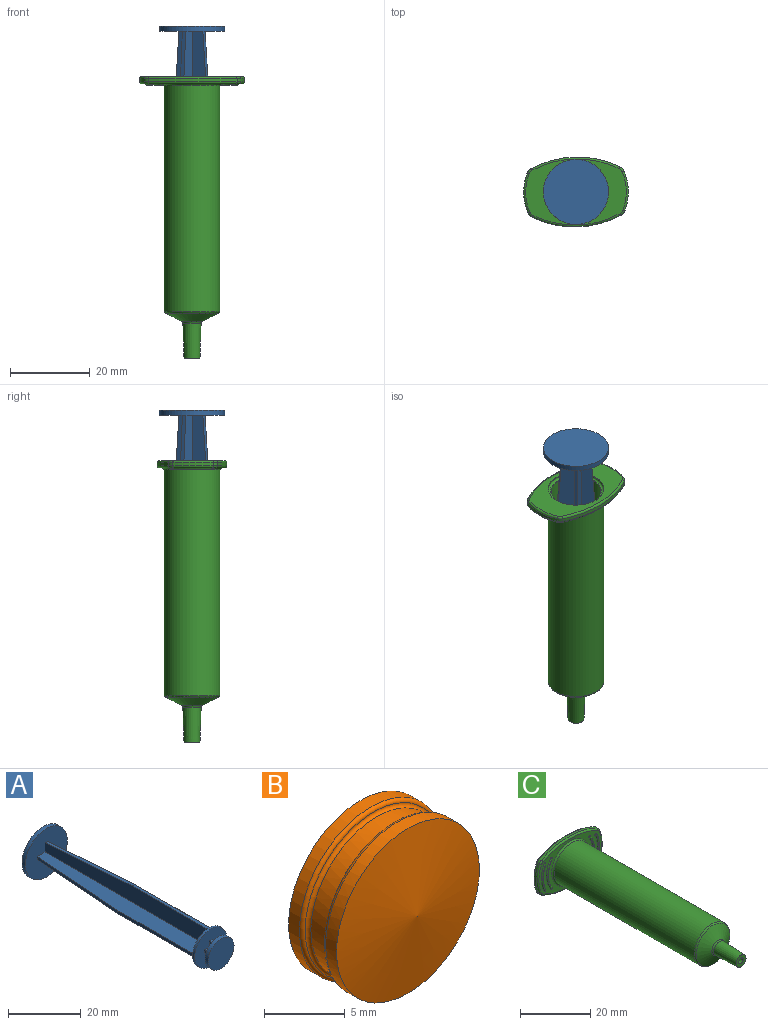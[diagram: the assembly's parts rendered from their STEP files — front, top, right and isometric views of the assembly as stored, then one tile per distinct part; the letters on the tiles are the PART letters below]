
ASSEMBLY  parts=3 mates=2
PART A: 37 faces, bbox 16.3x69x16.3 mm
  f0: plane 2.8x2mm, normal (-1,0,0), area 5.6mm2, adj f1,f10,f33,f34
  f1: plane 2.8x2mm, normal (0,0,-1), area 5.6mm2, adj f0,f11,f33,f34
  f2: plane 2.8x2mm, normal (0,0,-1), area 5.6mm2, adj f3,f9,f33,f34
  f3: plane 2.8x2mm, normal (1,0,0), area 5.6mm2, adj f2,f10,f33,f34
  f4: plane 2.8x2mm, normal (1,0,0), area 5.6mm2, adj f5,f8,f33,f34
  f5: plane 2.8x2mm, normal (0,0,1), area 5.6mm2, adj f4,f9,f33,f34
  f6: plane 2.8x2mm, normal (-1,0,0), area 5.6mm2, adj f7,f8,f33,f34
  f7: plane 2.8x2mm, normal (0,0,1), area 5.6mm2, adj f6,f11,f33,f34
  f8: plane 2.8x1mm, normal (0,0,1), area 2.8mm2, adj f4,f6,f33,f34
  f9: plane 2.8x1mm, normal (1,0,0), area 2.8mm2, adj f2,f5,f33,f34
  f10: plane 2.8x1mm, normal (0,0,-1), area 2.8mm2, adj f0,f3,f33,f34
  f11: plane 2.8x1mm, normal (-1,0,0), area 2.8mm2, adj f1,f7,f33,f34
  f12: plane 62.95x5.5mm, normal (0,0,1), area 305.7mm2, adj f15,f20,f24,f28,f32
  f13: plane 62.95x5.5mm, normal (0,0,-1), area 305.7mm2, adj f14,f20,f24,f28,f32
  f14: plane 62.95x5.5mm, normal (-1,0,0), area 305.7mm2, adj f13,f21,f25,f28,f32
  f15: plane 62.95x5.5mm, normal (-1,0,0), area 305.7mm2, adj f12,f23,f27,f28,f32
  f16: plane 62.95x5.5mm, normal (1,0,0), area 305.7mm2, adj f17,f21,f25,f28,f32
  f17: plane 62.95x5.5mm, normal (0,0,-1), area 305.7mm2, adj f16,f22,f26,f28,f32
  f18: plane 62.95x5.5mm, normal (0,0,1), area 305.7mm2, adj f19,f22,f26,f28,f32
  f19: plane 62.95x5.5mm, normal (1,0,0), area 305.7mm2, adj f18,f23,f27,f28,f32
  f20: plane 29.25x1mm, normal (-1,0,0), area 29.2mm2, adj f12,f13,f24,f32
  f21: plane 29.25x1mm, normal (0,0,-1), area 29.2mm2, adj f14,f16,f25,f32
  f22: plane 29.25x1mm, normal (1,0,0), area 29.2mm2, adj f17,f18,f26,f32
  f23: plane 29.25x1mm, normal (0,0,1), area 29.2mm2, adj f15,f19,f27,f32
  f24: plane 33.7x2.41mm, normal (-1,0.07,0), area 33.8mm2, adj f12,f13,f20,f28
  f25: plane 33.7x2.41mm, normal (0,0.07,-1), area 33.8mm2, adj f14,f16,f21,f28
  f26: plane 33.7x2.41mm, normal (1,0.07,0), area 33.8mm2, adj f17,f18,f22,f28
  f27: plane 33.7x2.41mm, normal (0,0.07,1), area 33.8mm2, adj f15,f19,f23,f28
  f28: plane 16.3x16.3mm, normal (0,-1,0), area 195.3mm2, adj f12,f13,f14,f15,f16,f17,f18,f19
  f29: cylinder r=8.15mm len=16.3mm, axis (0,1,0), area 66.6mm2, adj f28,f30
  f30: plane 16.3x16.3mm, normal (0,1,0), area 208.7mm2, adj f29
  f31: cylinder r=6.25mm len=12.5mm, axis (0,-1,0), area 29.5mm2, adj f32,f33
  f32: plane 12.5x12.5mm, normal (0,1,0), area 99.7mm2, adj f12,f13,f14,f15,f16,f17,f18,f19
  f33: plane 12.5x12.5mm, normal (0,-1,0), area 113.7mm2, adj f0,f1,f2,f3,f4,f5,f6,f7
  f34: plane 10x10mm, normal (0,1,0), area 69.5mm2, adj f0,f1,f2,f3,f4,f5,f6,f7
  f35: cylinder r=5mm len=10mm, axis (0,-1,0), area 37.7mm2, adj f34,f36
  f36: plane 10x10mm, normal (0,-1,0), area 78.5mm2, adj f35
PART B: 13 faces, bbox 13.5x5x13.5 mm
  f0: cone r=0mm half-angle=82.7deg, axis (0,1,0), area 123.7mm2, adj f1
  f1: cylinder r=6.25mm len=12.5mm, axis (0,-1,0), area 37.3mm2, adj f0,f10
  f2: cylinder r=5.75mm len=11.5mm, axis (0,-1,0), area 47mm2, adj f9,f12
  f3: cylinder r=6.25mm len=12.5mm, axis (0,-1,0), area 37.3mm2, adj f4,f11
  f4: plane 12.5x12.5mm, normal (0,1,0), area 103.1mm2, adj f3,f5
  f5: cylinder r=2.5mm len=5mm, axis (0,-1,0), area 44mm2, adj f4,f6
  f6: plane 10x10mm, normal (0,-1,0), area 58.9mm2, adj f5,f7
  f7: cylinder r=5mm len=10mm, axis (0,-1,0), area 37.7mm2, adj f6,f8
  f8: plane 10x10mm, normal (0,1,0), area 78.5mm2, adj f7
  f9: torus R=6mm, axis (0,1,0), area 14.4mm2, adj f2,f10
  f10: torus R=6mm, axis (0,1,0), area 15.2mm2, adj f1,f9
  f11: torus R=6mm, axis (0,-1,0), area 15.2mm2, adj f3,f12
  f12: torus R=6mm, axis (0,-1,0), area 14.4mm2, adj f2,f11
PART C: 75 faces, bbox 28.4x70.4x21.6 mm
  f0: plane 25.2x16.5mm, normal (0,-1,0), area 144mm2, adj f17,f18,f19,f20,f21,f22,f23,f24
  f1: plane 25.2x16.5mm, normal (0,1,0), area 197mm2, adj f12,f56,f57,f58,f59,f60,f61,f62
  f2: cylinder r=13.1mm len=10.15mm, axis (0,1,0), area 8.3mm2, adj f52,f53,f59,f67
  f3: plane 4x4mm, normal (0,-1,0), area 10mm2, adj f4,f8
  f4: cone r=2.3mm half-angle=1.9deg, axis (0,1,0), area 117.4mm2, adj f3,f72
  f5: cone r=7mm half-angle=62.9deg, axis (0,1,0), area 136.5mm2, adj f72,f73
  f6: cylinder r=7mm len=56.39mm, axis (0,1,0), area 2480.3mm2, adj f73,f74
  f7: cylinder r=13.1mm len=10.15mm, axis (0,1,0), area 8.3mm2, adj f51,f54,f60,f68
  f8: cone r=1.21mm half-angle=1.9deg, axis (0,1,0), area 61.6mm2, adj f3,f9
  f9: cone r=6.25mm half-angle=62.9deg, axis (0,1,0), area 132.6mm2, adj f8,f10
  f10: cylinder r=6.25mm len=57.79mm, axis (0,1,0), area 2269.4mm2, adj f9,f11
  f11: plane 13x13mm, normal (0,1,0), area 10mm2, adj f10,f55
  f12: cylinder r=7mm len=14mm, axis (0,1,0), area 11mm2, adj f1,f55
  f13: cylinder r=24.59mm len=22.28mm, axis (0,1,0), area 18.5mm2, adj f53,f54,f63,f71
  f14: cylinder r=24.59mm len=22.28mm, axis (0,1,0), area 18.5mm2, adj f51,f52,f56,f64
  f15: plane 9.38x1.11mm, normal (0,-1,0), area 1mm2, adj f18,f19,f22,f23
  f16: plane 10.37x1.66mm, normal (0,-1,0), area 1.1mm2, adj f26,f27,f30,f31
  f17: sphere r=0.3mm, area 0.1mm2, adj f0,f18,f19
  f18: torus R=11.3mm, axis (0,-1,0), area 4.6mm2, adj f0,f15,f17,f20
  f19: cylinder r=0.3mm len=0.31mm, axis (-0.9,0,0.44), area 0mm2, adj f0,f15,f17,f21
  f20: sphere r=0.3mm, area 0.1mm2, adj f0,f18,f22
  f21: sphere r=0.3mm, area 0.1mm2, adj f0,f19,f23
  f22: cylinder r=0.3mm len=0.31mm, axis (0.9,0,0.44), area 0mm2, adj f0,f15,f20,f24
  f23: torus R=11.2mm, axis (0,-1,0), area 4.4mm2, adj f0,f15,f21,f24
  f24: sphere r=0.3mm, area 0.1mm2, adj f0,f22,f23
  f25: sphere r=0.3mm, area 0.1mm2, adj f0,f26,f27
  f26: cylinder r=0.3mm len=0.3mm, axis (0.81,0,0.58), area 0mm2, adj f0,f16,f25,f28
  f27: torus R=9.29mm, axis (0,-1,0), area 5.3mm2, adj f0,f16,f25,f29
  f28: sphere r=0.3mm, area 0.1mm2, adj f0,f26,f30
  f29: sphere r=0.3mm, area 0.1mm2, adj f0,f27,f31
  f30: torus R=9.19mm, axis (0,-1,0), area 5mm2, adj f0,f16,f28,f32
  f31: cylinder r=0.3mm len=0.3mm, axis (-0.81,0,0.58), area 0mm2, adj f0,f16,f29,f32
  f32: sphere r=0.3mm, area 0.1mm2, adj f0,f30,f31
  f33: plane 9.38x1.11mm, normal (0,-1,0), area 1mm2, adj f36,f37,f40,f41
  f34: plane 10.37x1.66mm, normal (0,-1,0), area 1.1mm2, adj f44,f45,f48,f49
  f35: sphere r=0.3mm, area 0.1mm2, adj f0,f36,f37
  f36: cylinder r=0.3mm len=0.31mm, axis (-0.9,0,-0.44), area 0mm2, adj f0,f33,f35,f38
  f37: torus R=11.3mm, axis (0,-1,0), area 4.6mm2, adj f0,f33,f35,f39
  f38: sphere r=0.3mm, area 0.1mm2, adj f0,f36,f40
  f39: sphere r=0.3mm, area 0.1mm2, adj f0,f37,f41
  f40: torus R=11.2mm, axis (0,-1,0), area 4.4mm2, adj f0,f33,f38,f42
  f41: cylinder r=0.3mm len=0.31mm, axis (0.9,0,-0.44), area 0mm2, adj f0,f33,f39,f42
  f42: sphere r=0.3mm, area 0.1mm2, adj f0,f40,f41
  f43: sphere r=0.3mm, area 0.1mm2, adj f0,f44,f45
  f44: torus R=9.29mm, axis (0,-1,0), area 5.3mm2, adj f0,f34,f43,f46
  f45: cylinder r=0.3mm len=0.3mm, axis (0.81,0,-0.58), area 0mm2, adj f0,f34,f43,f47
  f46: sphere r=0.3mm, area 0.1mm2, adj f0,f44,f48
  f47: sphere r=0.3mm, area 0.1mm2, adj f0,f45,f49
  f48: cylinder r=0.3mm len=0.3mm, axis (-0.81,0,-0.58), area 0mm2, adj f0,f34,f46,f50
  f49: torus R=9.19mm, axis (0,-1,0), area 5mm2, adj f0,f34,f47,f50
  f50: sphere r=0.3mm, area 0.1mm2, adj f0,f48,f49
  f51: cylinder r=2mm len=1.01mm, axis (0,1,0), area 1.1mm2, adj f7,f14,f58,f66
  f52: cylinder r=2mm len=1.01mm, axis (0,1,0), area 1.1mm2, adj f2,f14,f57,f65
  f53: cylinder r=2mm len=1.01mm, axis (0,1,0), area 1.1mm2, adj f2,f13,f61,f69
  f54: cylinder r=2mm len=1.01mm, axis (0,1,0), area 1.1mm2, adj f7,f13,f62,f70
  f55: torus R=6.5mm, axis (0,-1,0), area 33.6mm2, adj f11,f12
  f56: torus R=24.09mm, axis (0,1,0), area 18mm2, adj f1,f14,f57,f58
  f57: torus R=1.5mm, axis (0,1,0), area 1mm2, adj f1,f52,f56,f59
  f58: torus R=1.5mm, axis (0,1,0), area 1mm2, adj f1,f51,f56,f60
  f59: torus R=12.6mm, axis (0,1,0), area 8.1mm2, adj f1,f2,f57,f61
  f60: torus R=12.6mm, axis (0,1,0), area 8.1mm2, adj f1,f7,f58,f62
  f61: torus R=1.5mm, axis (0,1,0), area 1mm2, adj f1,f53,f59,f63
  f62: torus R=1.5mm, axis (0,1,0), area 1mm2, adj f1,f54,f60,f63
  f63: torus R=24.09mm, axis (0,1,0), area 18mm2, adj f1,f13,f61,f62
  f64: torus R=24.09mm, axis (0,-1,0), area 18mm2, adj f0,f14,f65,f66
  f65: torus R=1.5mm, axis (0,-1,0), area 1mm2, adj f0,f52,f64,f67
  f66: torus R=1.5mm, axis (0,-1,0), area 1mm2, adj f0,f51,f64,f68
  f67: torus R=12.6mm, axis (0,-1,0), area 8.1mm2, adj f0,f2,f65,f69
  f68: torus R=12.6mm, axis (0,-1,0), area 8.1mm2, adj f0,f7,f66,f70
  f69: torus R=1.5mm, axis (0,-1,0), area 1mm2, adj f0,f53,f67,f71
  f70: torus R=1.5mm, axis (0,-1,0), area 1mm2, adj f0,f54,f68,f71
  f71: torus R=24.09mm, axis (0,-1,0), area 18mm2, adj f0,f13,f69,f70
  f72: torus R=2.79mm, axis (0,1,0), area 8mm2, adj f4,f5
  f73: torus R=6.5mm, axis (0,-1,0), area 23.8mm2, adj f5,f6
  f74: torus R=7.5mm, axis (0,-1,0), area 35.4mm2, adj f0,f6
PLACE A rot(axis=(0.21,0.69,0.69),156.4deg) t=(136.39,-55.32,67.1)mm
PLACE B rot(axis=(-1,-0.01,0.01),90deg) t=(136.39,-55.32,31.1)mm
PLACE C rot(axis=(1,0.01,0.01),90deg) t=(136.39,-55.32,103.4)mm
MATE revolute A.f29 <-> C.f2  axis (0,0,1) through (136.39,-55.32,116.1)mm
MATE revolute B.f0 <-> A.f35  axis (0,0,-1) through (136.39,-55.32,47.1)mm
